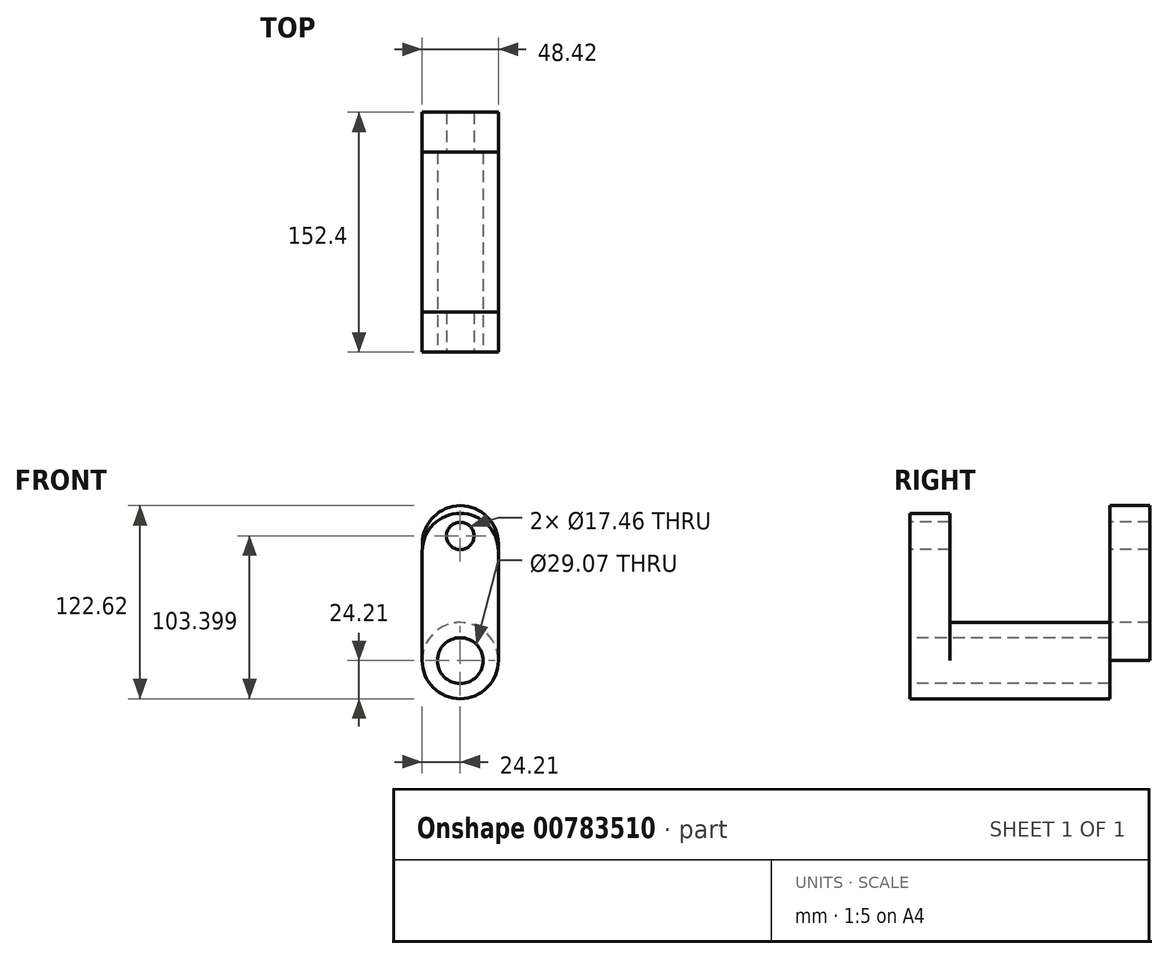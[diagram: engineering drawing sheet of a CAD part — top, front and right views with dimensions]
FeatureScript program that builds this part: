
annotation { "Feature Type Name" : "Feature", "Feature Type Description" : "" }
export const myFeature = defineFeature(function(context is Context, id is Id, definition is map)
    precondition{}
    {
        {
            var Q0;
            Q0=qCreatedBy(makeId("Front.planeOp"),FACE);
            var sketch = newSketch(context, id + "F0", { "sketchPlane" : qUnion([Q0])});
            skCircle(sketch, "E0", {"center": v(0, 0) * mm, "radius": 24.21 * mm});
            skSolve(sketch);
        }
        {
            var Q0;
            Q0=makeQuery(id+"F0.imprint","IMPRINT",FACE,{"disambiguationData":[TD([[makeQuery(id+"F0.imprint","IMPRINT",EDGE,{"derivedFrom":sQuery(id+"F0.wireOp",EDGE,"E0")}),1.0]])]});
            extrude(context, id + "F1", {"entities" : qUnion([Q0]), "depth" : 101.6 * mm, "offsetDistance" : 25.4 * mm});
        }
        {
            var Q0;
            Q0=makeQuery(id+"F1.opExtrude","CAP_FACE",FACE,{"disambiguationData":[OSD([sQuery(id+"F0.wireOp",EDGE,"E0")])],"isStart":false});
            var sketch = newSketch(context, id + "F2", { "sketchPlane" : qUnion([Q0])});
            skLineSegment(sketch, "E1", {"start": v(-24.21, 0) * mm, "end": v(-24.21, 69.35) * mm});
            skLineSegment(sketch, "E2", {"start": v(24.21, 0) * mm, "end": v(24.21, 69.35) * mm});
            skArc(sketch, "E3", {"start": v(24.21, 69.35) * mm, "mid": v(0, 93.57) * mm, "end": v(-24.21, 69.35) * mm});
            skSolve(sketch);
        }
        {
            var Q0;
            {var subQ0=sQuery(id+"F2.wireOp",EDGE,"E1");Q0=makeQuery(id+"F2.imprint","IMPRINT",FACE,{"disambiguationData":[TD([[makeQuery(id+"F2.imprint","IMPRINT",EDGE,{"derivedFrom":subQ0}),-1.0]])]});}
            var Q1;
            {var subQ0=makeQuery(id+"F1.opExtrude","CAP_EDGE",EDGE,{"disambiguationData":[OSD([sQuery(id+"F0.wireOp",EDGE,"E0")])],"isStart":false});var subQ1=makeQuery(id+"F2.imprint","INTERSECT",VERTEX,{"derivedFrom":[subQ0,sQuery(id+"F2.wireOp",EDGE,"E1")]});Q1=makeQuery(id+"F2.imprint","IMPRINT",FACE,{"disambiguationData":[TD([[makeQuery(id+"F2.imprint","IMPRINT",EDGE,{"disambiguationData":[TD([[subQ1,-1.0]])],"derivedFrom":subQ0}),1.0]])]});}
            extrude(context, id + "F3", {"entities" : qUnion([Q0, Q1]), "operationType" : NewBodyOperationType.ADD, "depth" : 25.4 * mm, "offsetDistance" : 25.4 * mm});
        }
        {
            var Q0;
            Q0=makeQuery(id+"F1.opExtrude","CAP_FACE",FACE,{"disambiguationData":[OSD([sQuery(id+"F0.wireOp",EDGE,"E0")])],"isStart":true});
            var sketch = newSketch(context, id + "F4", { "sketchPlane" : qUnion([Q0])});
            skLineSegment(sketch, "E4", {"start": v(-24.21, 0) * mm, "end": v(-24.21, 74.37) * mm});
            skLineSegment(sketch, "E5", {"start": v(-24.21, 74.37) * mm, "end": v(24, 74.37) * mm});
            skLineSegment(sketch, "E6", {"start": v(24, 74.37) * mm, "end": v(24.21, 0) * mm});
            skArc(sketch, "E7", {"start": v(24, 74.37) * mm, "mid": v(-0.1, 98.41) * mm, "end": v(-24.21, 74.37) * mm});
            skSolve(sketch);
        }
        {
            var Q0;
            Q0=makeQuery(id+"F4.imprint","IMPRINT",FACE,{"disambiguationData":[TD([[makeQuery(id+"F4.imprint","IMPRINT",EDGE,{"derivedFrom":sQuery(id+"F4.wireOp",EDGE,"E5")}),1.0]])]});
            var Q1;
            {var subQ0=sQuery(id+"F4.wireOp",EDGE,"E4");Q1=makeQuery(id+"F4.imprint","IMPRINT",FACE,{"disambiguationData":[TD([[makeQuery(id+"F4.imprint","IMPRINT",EDGE,{"derivedFrom":subQ0}),-1.0]])]});}
            var Q2;
            {var subQ0=sQuery(id+"F4.wireOp",EDGE,"E6");var subQ1=makeQuery(id+"F1.opExtrude","CAP_EDGE",EDGE,{"disambiguationData":[OSD([sQuery(id+"F0.wireOp",EDGE,"E0")])],"isStart":true});var subQ2=makeQuery(id+"F4.imprint","INTERSECT",VERTEX,{"disambiguationData":[OD(0.0)],"derivedFrom":[subQ1,subQ0]});Q2=makeQuery(id+"F4.imprint","IMPRINT",FACE,{"disambiguationData":[TD([[makeQuery(id+"F4.imprint","IMPRINT",EDGE,{"disambiguationData":[TD([[subQ2,1.0]])],"derivedFrom":subQ0}),-1.0]])]});}
            extrude(context, id + "F5", {"entities" : qUnion([Q0, Q1, Q2]), "operationType" : NewBodyOperationType.ADD, "depth" : 25.4 * mm, "offsetDistance" : 25.4 * mm});
        }
        {
            var Q0;
            Q0=makeQuery(id+"F3.opExtrude","CAP_FACE",FACE,{"disambiguationData":[OSD([sQuery(id+"F0.wireOp",EDGE,"E0"),sQuery(id+"F2.wireOp",EDGE,"E1"),sQuery(id+"F2.wireOp",EDGE,"E2"),sQuery(id+"F2.wireOp",EDGE,"E3")])],"isStart":false});
            var sketch = newSketch(context, id + "F6", { "sketchPlane" : qUnion([Q0])});
            skCircle(sketch, "E8", {"center": v(0, 0) * mm, "radius": 14.53 * mm});
            skCircle(sketch, "E9", {"center": v(0, 79.19) * mm, "radius": 8.73 * mm});
            skSolve(sketch);
        }
        {
            var Q0;
            Q0=makeQuery(id+"F6.imprint","IMPRINT",FACE,{"disambiguationData":[TD([[makeQuery(id+"F6.imprint","IMPRINT",EDGE,{"derivedFrom":sQuery(id+"F6.wireOp",EDGE,"E9")}),1.0]])]});
            var Q1;
            Q1=makeQuery(id+"F6.imprint","IMPRINT",FACE,{"disambiguationData":[TD([[makeQuery(id+"F6.imprint","IMPRINT",EDGE,{"derivedFrom":sQuery(id+"F6.wireOp",EDGE,"E8")}),1.0]])]});
            extrude(context, id + "F7", {"entities" : qUnion([Q0, Q1]), "operationType" : NewBodyOperationType.REMOVE, "oppositeDirection" : true, "depth" : 254 * mm, "offsetDistance" : 25.4 * mm});
        }
    });
